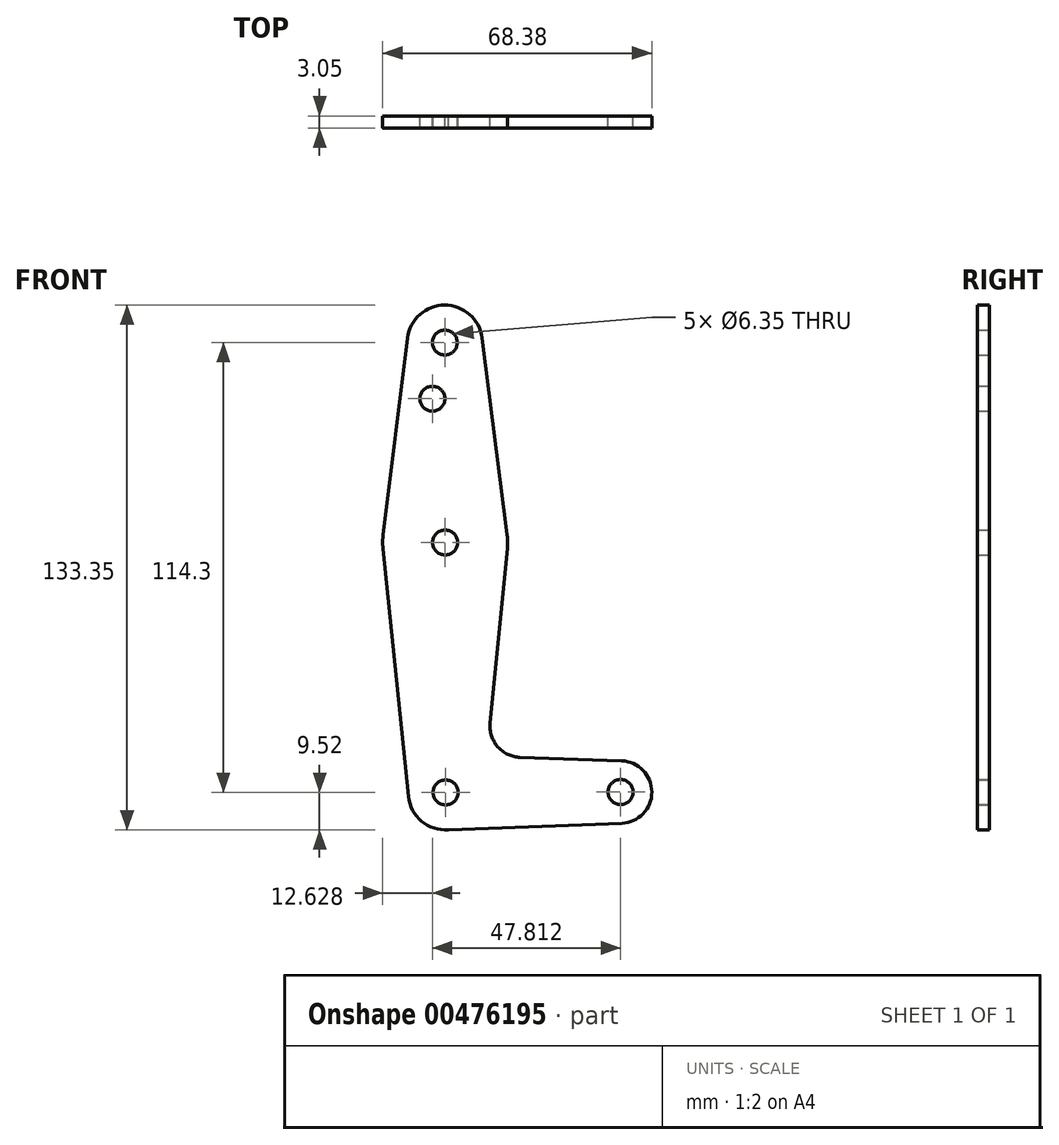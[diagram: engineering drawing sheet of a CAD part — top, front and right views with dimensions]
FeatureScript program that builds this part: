
annotation { "Feature Type Name" : "Feature", "Feature Type Description" : "" }
export const myFeature = defineFeature(function(context is Context, id is Id, definition is map)
    precondition{}
    {
        {
            var Q0;
            Q0=qCreatedBy(makeId("Front.planeOp"),FACE);
            var sketch = newSketch(context, id + "F0", { "sketchPlane" : qUnion([Q0])});
            skLineSegment(sketch, "E0", {"start": v(0, 0) * mm, "end": v(44.45, 0.08) * mm, "construction": true});
            skLineSegment(sketch, "E1", {"start": v(0, 0) * mm, "end": v(-0.21, 114.3) * mm, "construction": true});
            skCircle(sketch, "E2", {"center": v(-0.21, 114.3) * mm, "radius": 9.53 * mm});
            skCircle(sketch, "E3", {"center": v(0, 0) * mm, "radius": 9.53 * mm});
            skCircle(sketch, "E4", {"center": v(44.45, 0.08) * mm, "radius": 7.94 * mm});
            skCircle(sketch, "E5", {"center": v(-0.12, 63.5) * mm, "radius": 15.88 * mm});
            skLineSegment(sketch, "E6", {"start": v(18.95, 8.89) * mm, "end": v(44.72, 8.02) * mm});
            skLineSegment(sketch, "E7", {"start": v(0, -9.53) * mm, "end": v(44.75, -7.85) * mm});
            skLineSegment(sketch, "E8", {"start": v(-9.67, 115.47) * mm, "end": v(-15.87, 65.45) * mm});
            skLineSegment(sketch, "E9", {"start": v(-15.91, 61.88) * mm, "end": v(-9.48, -0.97) * mm});
            skLineSegment(sketch, "E10", {"start": v(15.68, 61.94) * mm, "end": v(11.3, 17.61) * mm});
            skLineSegment(sketch, "E11", {"start": v(9.23, 115.5) * mm, "end": v(15.63, 65.51) * mm});
            skArc(sketch, "E12.filletArc", {"start": v(11.3, 17.61) * mm, "mid": v(13.24, 11.6) * mm, "end": v(18.95, 8.89) * mm});
            skCircle(sketch, "E13", {"center": v(-0.21, 114.3) * mm, "radius": 3.18 * mm});
            skCircle(sketch, "E14", {"center": v(-0.12, 63.5) * mm, "radius": 3.18 * mm});
            skCircle(sketch, "E15", {"center": v(0, 0) * mm, "radius": 3.18 * mm});
            skCircle(sketch, "E16", {"center": v(44.45, 0.08) * mm, "radius": 3.18 * mm});
            skCircle(sketch, "E17", {"center": v(-3.36, 100.03) * mm, "radius": 3.18 * mm});
            skSolve(sketch);
        }
        {
            var Q0;
            Q0 = qSketchRegion(id + "F0", true);
            extrude(context, id + "F1", {"entities" : qUnion([Q0]), "depth" : 3.05 * mm});
        }
    });
